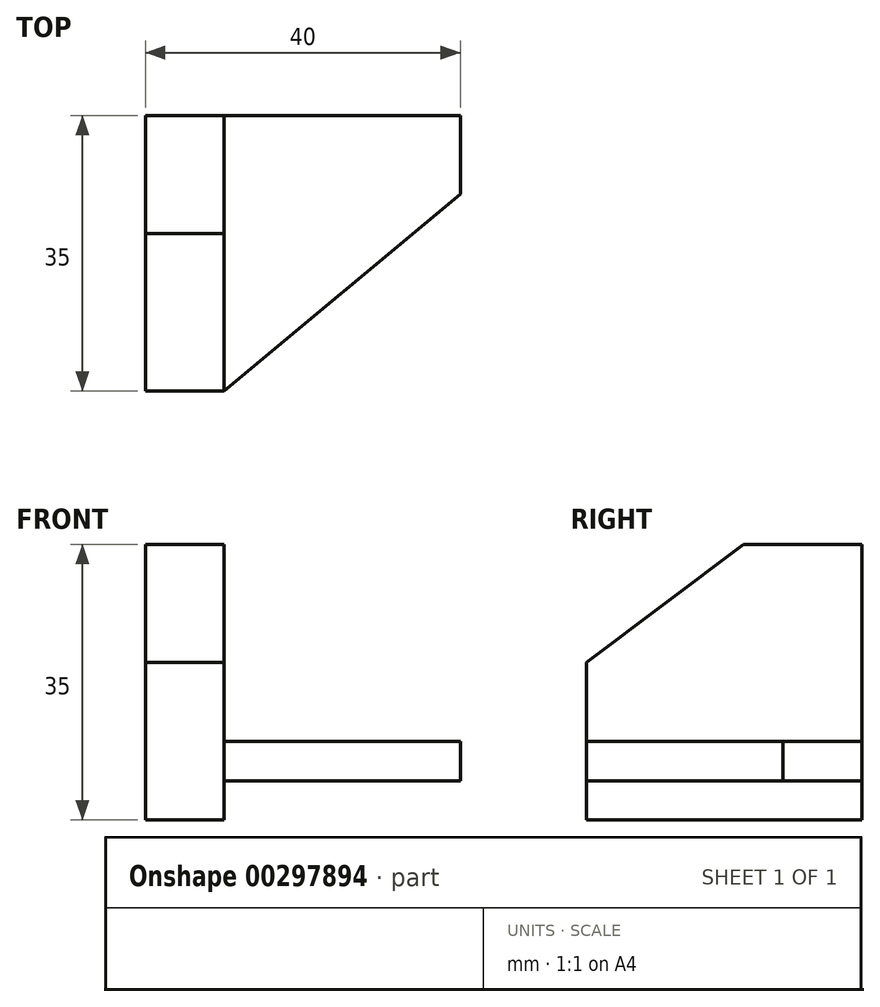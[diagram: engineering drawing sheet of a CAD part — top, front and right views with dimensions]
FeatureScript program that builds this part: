
annotation { "Feature Type Name" : "Feature", "Feature Type Description" : "" }
export const myFeature = defineFeature(function(context is Context, id is Id, definition is map)
    precondition{}
    {
        {
            var Q0;
            Q0=qCreatedBy(makeId("Front.planeOp"),FACE);
            var sketch = newSketch(context, id + "F0", { "sketchPlane" : qUnion([Q0])});
            skLineSegment(sketch, "E0.bottom", {"start": v(-32.92, 30) * mm, "end": v(32.08, 30) * mm});
            skLineSegment(sketch, "E0.top", {"start": v(-32.92, -10) * mm, "end": v(32.08, -10) * mm});
            skLineSegment(sketch, "E0.left", {"start": v(-32.92, 30) * mm, "end": v(-32.92, -10) * mm});
            skLineSegment(sketch, "E0.right", {"start": v(32.08, 30) * mm, "end": v(32.08, -10) * mm});
            skLineSegment(sketch, "E1.bottom", {"start": v(-32.92, 25) * mm, "end": v(-22.92, 25) * mm});
            skLineSegment(sketch, "E1.top", {"start": v(-32.92, -10) * mm, "end": v(-22.92, -10) * mm});
            skLineSegment(sketch, "E1.left", {"start": v(-32.92, 25) * mm, "end": v(-32.92, -10) * mm});
            skLineSegment(sketch, "E1.right", {"start": v(-22.92, 25) * mm, "end": v(-22.92, -10) * mm});
            skLineSegment(sketch, "E2.left", {"start": v(-22.92, 7.5) * mm, "end": v(-22.92, -5) * mm});
            skCircle(sketch, "E3", {"center": v(15.02, 0) * mm, "radius": 5 * mm});
            skLineSegment(sketch, "E4", {"start": v(-7.92, 30) * mm, "end": v(32.08, 10) * mm});
            skLineSegment(sketch, "E5.bottom", {"start": v(-22.92, -5) * mm, "end": v(7.08, -5) * mm});
            skLineSegment(sketch, "E5.top", {"start": v(-22.92, 0) * mm, "end": v(7.08, 0) * mm});
            skLineSegment(sketch, "E5.left", {"start": v(-22.92, -5) * mm, "end": v(-22.92, 0) * mm});
            skLineSegment(sketch, "E5.right", {"start": v(7.08, -5) * mm, "end": v(7.08, 0) * mm});
            skSolve(sketch);
        }
        {
            var Q0;
            {var subQ1=sQuery(id+"F0.wireOp",EDGE,"E0.top");Q0=makeQuery(id+"F0.imprint","IMPRINT",FACE,{"disambiguationData":[TD([[makeQuery(id+"F0.imprint","IMPRINT",EDGE,{"derivedFrom":subQ1}),1.0]])]});}
            extrude(context, id + "F1", {"entities" : qUnion([Q0]), "depth" : 10 * mm});
        }
        {
            var Q0;
            {var subQ1=sQuery(id+"F0.wireOp",EDGE,"E1.bottom");Q0=makeQuery(id+"F0.imprint","IMPRINT",FACE,{"disambiguationData":[TD([[makeQuery(id+"F0.imprint","IMPRINT",EDGE,{"derivedFrom":subQ1}),-1.0]])]});}
            var Q1;
            Q1=makeQuery(id+"F0.imprint","IMPRINT",FACE,{"disambiguationData":[TD([[makeQuery(id+"F0.imprint","IMPRINT",EDGE,{"derivedFrom":sQuery(id+"F0.wireOp",EDGE,"E5.bottom")}),1.0]])]});
            extrude(context, id + "F2", {"entities" : qUnion([Q0, Q1]), "operationType" : NewBodyOperationType.ADD, "depth" : 35 * mm});
        }
        {
            var Q0;
            Q0=makeQuery(id+"F2.boolean.opBoolean","MERGE",FACE,{"derivedFrom":[makeQuery(id+"F1.opExtrude","SWEPT_FACE",FACE,{"disambiguationData":[OSD([sQuery(id+"F0.wireOp",EDGE,"E0.left")])]}),makeQuery(id+"F2.opExtrude","SWEPT_FACE",FACE,{"disambiguationData":[OSD([sQuery(id+"F0.wireOp",EDGE,"E1.left")])]})]});
            var sketch = newSketch(context, id + "F3", { "sketchPlane" : qUnion([Q0])});
            skLineSegment(sketch, "E6", {"start": v(15, 25) * mm, "end": v(35, 10) * mm});
            skSolve(sketch);
        }
        {
            var Q0;
            {var subQ0=sQuery(id+"F3.wireOp",EDGE,"E6");Q0=makeQuery(id+"F3.imprint","IMPRINT",FACE,{"disambiguationData":[TD([[makeQuery(id+"F3.imprint","IMPRINT",EDGE,{"derivedFrom":subQ0}),1.0]])]});}
            extrude(context, id + "F4", {"entities" : qUnion([Q0]), "operationType" : NewBodyOperationType.REMOVE, "oppositeDirection" : true, "depth" : 10 * mm});
        }
        {
            var Q0;
            Q0=makeQuery(id+"F2.opExtrude","SWEPT_FACE",FACE,{"disambiguationData":[OSD([sQuery(id+"F0.wireOp",EDGE,"E5.top")])]});
            var sketch = newSketch(context, id + "F5", { "sketchPlane" : qUnion([Q0])});
            skLineSegment(sketch, "E7", {"start": v(-22.92, -35) * mm, "end": v(7.08, -10) * mm});
            skSolve(sketch);
        }
        {
            var Q0;
            Q0=makeQuery(id+"F5.imprint","IMPRINT",FACE,{"disambiguationData":[TD([[makeQuery(id+"F5.imprint","IMPRINT",EDGE,{"derivedFrom":sQuery(id+"F5.wireOp",EDGE,"E7")}),-1.0]])]});
            extrude(context, id + "F6", {"entities" : qUnion([Q0]), "operationType" : NewBodyOperationType.REMOVE, "oppositeDirection" : true, "depth" : 10 * mm});
        }
    });
